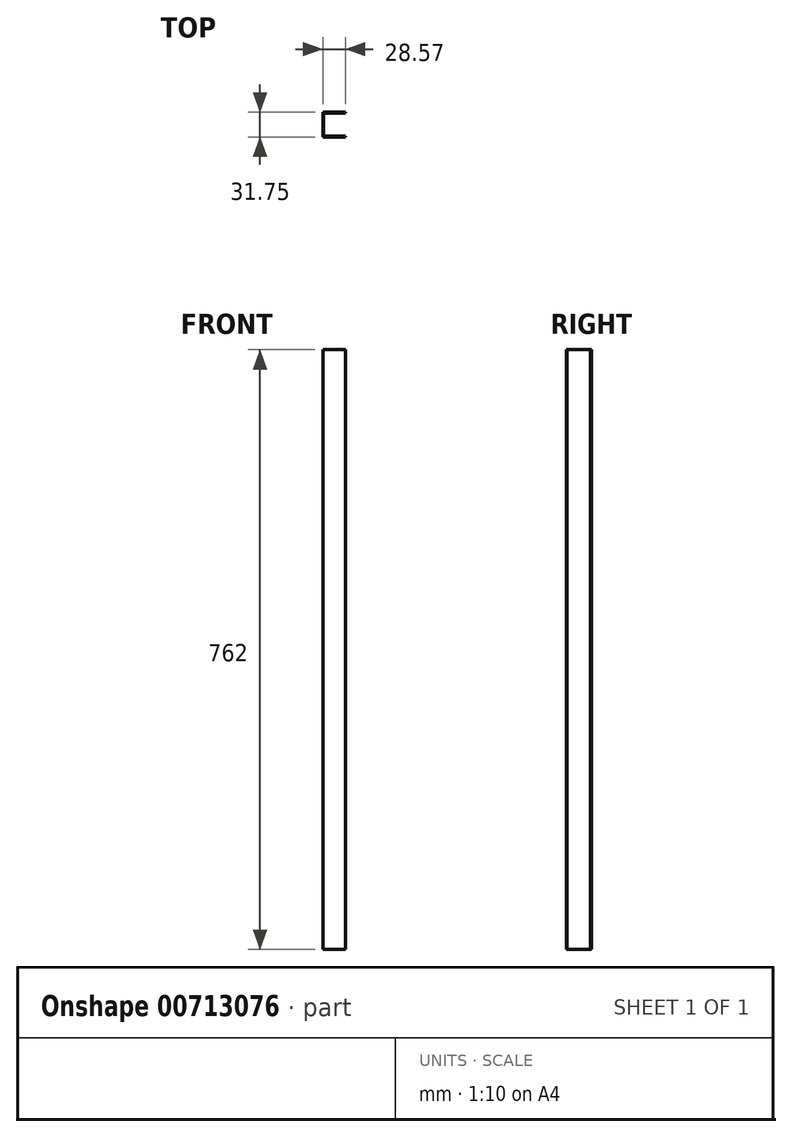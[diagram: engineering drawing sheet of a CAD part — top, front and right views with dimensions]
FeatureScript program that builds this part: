
annotation { "Feature Type Name" : "Feature", "Feature Type Description" : "" }
export const myFeature = defineFeature(function(context is Context, id is Id, definition is map)
    precondition{}
    {
        {
            var Q0;
            Q0=qCreatedBy(makeId("Top.planeOp"),FACE);
            var sketch = newSketch(context, id + "F0", { "sketchPlane" : qUnion([Q0])});
            skLineSegment(sketch, "E0.bottom", {"start": v(-88.71, 54.73) * mm, "end": v(-60.14, 54.73) * mm});
            skLineSegment(sketch, "E0.top", {"start": v(-88.71, 22.98) * mm, "end": v(-60.14, 22.98) * mm});
            skLineSegment(sketch, "E0.left", {"start": v(-88.71, 54.73) * mm, "end": v(-88.71, 22.98) * mm});
            skLineSegment(sketch, "E0.right", {"start": v(-60.14, 54.73) * mm, "end": v(-60.14, 22.98) * mm});
            skLineSegment(sketch, "E1.bottom", {"start": v(-87.68, 24) * mm, "end": v(-57.77, 24) * mm});
            skLineSegment(sketch, "E1.top", {"start": v(-87.68, 53.66) * mm, "end": v(-57.77, 53.66) * mm});
            skLineSegment(sketch, "E1.left", {"start": v(-87.68, 24) * mm, "end": v(-87.68, 53.66) * mm});
            skLineSegment(sketch, "E1.right", {"start": v(-57.77, 24) * mm, "end": v(-57.77, 53.66) * mm});
            skSolve(sketch);
        }
        {
            var Q0;
            {var subQ1=sQuery(id+"F0.wireOp",EDGE,"E0.bottom");Q0=makeQuery(id+"F0.imprint","IMPRINT",FACE,{"disambiguationData":[TD([[makeQuery(id+"F0.imprint","IMPRINT",EDGE,{"derivedFrom":subQ1}),-1.0]])]});}
            extrude(context, id + "F1", {"entities" : qUnion([Q0]), "depth" : 762 * mm});
        }
    });
